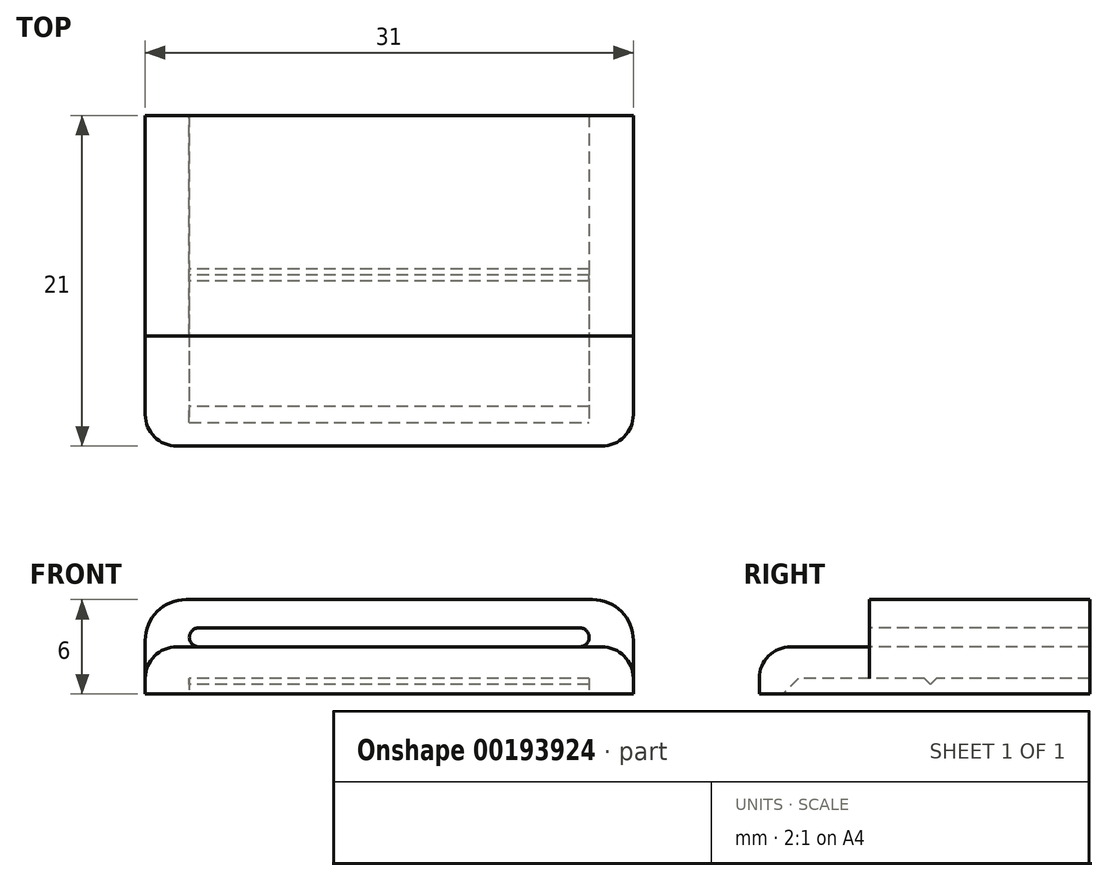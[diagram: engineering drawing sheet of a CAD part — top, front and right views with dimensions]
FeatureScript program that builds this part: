
annotation { "Feature Type Name" : "Feature", "Feature Type Description" : "" }
export const myFeature = defineFeature(function(context is Context, id is Id, definition is map)
    precondition{}
    {
        {
            var Q0;
            Q0=qCreatedBy(makeId("Top.planeOp"),FACE);
            var sketch = newSketch(context, id + "F0", { "sketchPlane" : qUnion([Q0])});
            skLineSegment(sketch, "E0.bottom", {"start": v(15.5, 10.5) * mm, "end": v(-15.5, 10.5) * mm});
            skLineSegment(sketch, "E0.top", {"start": v(15.5, -10.5) * mm, "end": v(-15.5, -10.5) * mm});
            skLineSegment(sketch, "E0.left", {"start": v(15.5, 10.5) * mm, "end": v(15.5, -10.5) * mm});
            skLineSegment(sketch, "E0.right", {"start": v(-15.5, 10.5) * mm, "end": v(-15.5, -10.5) * mm});
            skPoint(sketch, "E0.middle", {"position": v(0, 0) * mm});
            skSolve(sketch);
        }
        {
            var Q0;
            Q0 = qSketchRegion(id + "F0", true);
            extrude(context, id + "F1", {"entities" : qUnion([Q0]), "depth" : 3 * mm});
        }
        {
            var Q0;
            Q0=makeQuery(id+"F1.opExtrude","CAP_FACE",FACE,{"disambiguationData":[OSD([sQuery(id+"F0.wireOp",EDGE,"E0.bottom"),sQuery(id+"F0.wireOp",EDGE,"E0.top"),sQuery(id+"F0.wireOp",EDGE,"E0.left"),sQuery(id+"F0.wireOp",EDGE,"E0.right")])],"isStart":false});
            var sketch = newSketch(context, id + "F2", { "sketchPlane" : qUnion([Q0])});
            skLineSegment(sketch, "E1.bottom", {"start": v(-15.5, 10.5) * mm, "end": v(15.5, 10.5) * mm});
            skLineSegment(sketch, "E1.top", {"start": v(-15.5, -3.5) * mm, "end": v(15.5, -3.5) * mm});
            skLineSegment(sketch, "E1.left", {"start": v(-15.5, 10.5) * mm, "end": v(-15.5, -3.5) * mm});
            skLineSegment(sketch, "E1.right", {"start": v(15.5, 10.5) * mm, "end": v(15.5, -3.5) * mm});
            skSolve(sketch);
        }
        {
            var Q0;
            Q0 = qSketchRegion(id + "F2", true);
            extrude(context, id + "F3", {"entities" : qUnion([Q0]), "operationType" : NewBodyOperationType.ADD, "depth" : 3 * mm});
        }
        {
            var Q0;
            Q0=makeQuery(id+"F3.opExtrude","SWEPT_FACE",FACE,{"disambiguationData":[OSD([sQuery(id+"F2.wireOp",EDGE,"E1.top")])]});
            var sketch = newSketch(context, id + "F4", { "sketchPlane" : qUnion([Q0])});
            skLineSegment(sketch, "E2.bottom", {"start": v(-12.7, 3) * mm, "end": v(12.7, 3) * mm});
            skLineSegment(sketch, "E2.top", {"start": v(-12.7, 4.2) * mm, "end": v(12.7, 4.2) * mm});
            skLineSegment(sketch, "E2.left", {"start": v(-12.7, 3) * mm, "end": v(-12.7, 4.2) * mm});
            skLineSegment(sketch, "E2.right", {"start": v(12.7, 3) * mm, "end": v(12.7, 4.2) * mm});
            skSolve(sketch);
        }
        {
            var Q0;
            Q0 = qSketchRegion(id + "F4", true);
            extrude(context, id + "F5", {"entities" : qUnion([Q0]), "operationType" : NewBodyOperationType.REMOVE, "oppositeDirection" : true, "depth" : 25 * mm});
        }
        {
            var Q0;
            Q0=makeQuery(id+"F1.opExtrude","CAP_FACE",FACE,{"disambiguationData":[OSD([sQuery(id+"F0.wireOp",EDGE,"E0.bottom"),sQuery(id+"F0.wireOp",EDGE,"E0.top"),sQuery(id+"F0.wireOp",EDGE,"E0.left"),sQuery(id+"F0.wireOp",EDGE,"E0.right")])],"isStart":true});
            var sketch = newSketch(context, id + "F6", { "sketchPlane" : qUnion([Q0])});
            skLineSegment(sketch, "E3.bottom", {"start": v(-12.7, -10.5) * mm, "end": v(12.7, -10.5) * mm});
            skLineSegment(sketch, "E3.top", {"start": v(-12.7, 9) * mm, "end": v(12.7, 9) * mm});
            skLineSegment(sketch, "E3.left", {"start": v(-12.7, -10.5) * mm, "end": v(-12.7, 9) * mm});
            skLineSegment(sketch, "E3.right", {"start": v(12.7, -10.5) * mm, "end": v(12.7, 9) * mm});
            skSolve(sketch);
        }
        {
            var Q0;
            Q0 = qSketchRegion(id + "F6", true);
            extrude(context, id + "F7", {"entities" : qUnion([Q0]), "operationType" : NewBodyOperationType.REMOVE, "oppositeDirection" : true, "depth" : 1 * mm});
        }
        {
            var Q0;
            Q0=makeQuery(id+"F5.boolean.opBoolean","COPY",EDGE,{"derivedFrom":makeQuery(id+"F5.opExtrude","SWEPT_EDGE",EDGE,{"disambiguationData":[OSD([sQuery(id+"F4.wireOp",EDGE,"E2.top"),sQuery(id+"F4.wireOp",EDGE,"E2.right")])]})});
            var Q1;
            Q1=makeQuery(id+"F5.boolean.opBoolean","COPY",EDGE,{"derivedFrom":makeQuery(id+"F5.opExtrude","SWEPT_EDGE",EDGE,{"disambiguationData":[OSD([sQuery(id+"F2.wireOp",EDGE,"E1.top"),sQuery(id+"F4.wireOp",EDGE,"E2.bottom"),sQuery(id+"F4.wireOp",EDGE,"E2.right")])]})});
            var Q2;
            Q2=makeQuery(id+"F5.boolean.opBoolean","COPY",EDGE,{"derivedFrom":makeQuery(id+"F5.opExtrude","SWEPT_EDGE",EDGE,{"disambiguationData":[OSD([sQuery(id+"F2.wireOp",EDGE,"E1.top"),sQuery(id+"F4.wireOp",EDGE,"E2.bottom"),sQuery(id+"F4.wireOp",EDGE,"E2.left")])]})});
            var Q3;
            Q3=makeQuery(id+"F5.boolean.opBoolean","COPY",EDGE,{"derivedFrom":makeQuery(id+"F5.opExtrude","SWEPT_EDGE",EDGE,{"disambiguationData":[OSD([sQuery(id+"F4.wireOp",EDGE,"E2.top"),sQuery(id+"F4.wireOp",EDGE,"E2.left")])]})});
            fillet(context, id + "F8", {"entities" : qUnion([Q0, Q1, Q2, Q3]), "radius" : 0.6 * mm, "tangentPropagation" : true, "allowEdgeOverflow" : false});
        }
        {
            var Q0;
            Q0=makeQuery(id+"F3.opExtrude","CAP_EDGE",EDGE,{"disambiguationData":[OSD([sQuery(id+"F2.wireOp",EDGE,"E1.left")])],"isStart":false});
            var Q1;
            Q1=makeQuery(id+"F3.opExtrude","CAP_EDGE",EDGE,{"disambiguationData":[OSD([sQuery(id+"F2.wireOp",EDGE,"E1.right")])],"isStart":false});
            fillet(context, id + "F9", {"entities" : qUnion([Q0, Q1]), "radius" : 2.6 * mm, "tangentPropagation" : true, "allowEdgeOverflow" : false});
        }
        {
            var Q0;
            Q0=makeQuery(id+"F7.boolean.opBoolean","COPY",FACE,{"derivedFrom":makeQuery(id+"F7.opExtrude","CAP_FACE",FACE,{"disambiguationData":[OSD([sQuery(id+"F6.wireOp",EDGE,"E3.bottom"),sQuery(id+"F6.wireOp",EDGE,"E3.top"),sQuery(id+"F6.wireOp",EDGE,"E3.left"),sQuery(id+"F6.wireOp",EDGE,"E3.right")])],"isStart":false})});
            var sketch = newSketch(context, id + "F10", { "sketchPlane" : qUnion([Q0])});
            skLineSegment(sketch, "E4.bottom", {"start": v(12.7, -0.75) * mm, "end": v(-12.7, -0.75) * mm});
            skLineSegment(sketch, "E4.top", {"start": v(12.7, 0) * mm, "end": v(-12.7, 0) * mm});
            skLineSegment(sketch, "E4.left", {"start": v(12.7, -0.75) * mm, "end": v(12.7, 0) * mm});
            skLineSegment(sketch, "E4.right", {"start": v(-12.7, -0.75) * mm, "end": v(-12.7, 0) * mm});
            skSolve(sketch);
        }
        {
            var Q0;
            Q0 = qSketchRegion(id + "F10", true);
            extrude(context, id + "F11", {"entities" : qUnion([Q0]), "operationType" : NewBodyOperationType.ADD, "depth" : 0.5 * mm});
        }
        {
            var Q0;
            Q0=makeQuery(id+"F11.opExtrude","CAP_EDGE",EDGE,{"disambiguationData":[OSD([sQuery(id+"F10.wireOp",EDGE,"E4.top")])],"isStart":false});
            var Q1;
            Q1=makeQuery(id+"F11.opExtrude","CAP_EDGE",EDGE,{"disambiguationData":[OSD([sQuery(id+"F10.wireOp",EDGE,"E4.bottom")])],"isStart":false});
            chamfer(context, id + "F12", {"entities" : qUnion([Q0, Q1]), "width" : 0.5 * mm, "tangentPropagation" : true});
        }
        {
            var Q0;
            Q0=makeQuery(id+"F1.opExtrude","SWEPT_EDGE",EDGE,{"disambiguationData":[OSD([sQuery(id+"F0.wireOp",EDGE,"E0.top"),sQuery(id+"F0.wireOp",EDGE,"E0.left")])]});
            var Q1;
            Q1=makeQuery(id+"F1.opExtrude","SWEPT_EDGE",EDGE,{"disambiguationData":[OSD([sQuery(id+"F0.wireOp",EDGE,"E0.top"),sQuery(id+"F0.wireOp",EDGE,"E0.right")])]});
            fillet(context, id + "F13", {"entities" : qUnion([Q0, Q1]), "radius" : 2 * mm, "tangentPropagation" : true, "allowEdgeOverflow" : false});
        }
        {
            var Q0;
            Q0=makeQuery(id+"F7.boolean.opBoolean","COPY",EDGE,{"derivedFrom":makeQuery(id+"F7.opExtrude","CAP_EDGE",EDGE,{"disambiguationData":[OSD([sQuery(id+"F6.wireOp",EDGE,"E3.top")])],"isStart":false})});
            chamfer(context, id + "F14", {"entities" : qUnion([Q0]), "width" : 1 * mm, "tangentPropagation" : true});
        }
        {
            var Q0;
            Q0=makeQuery(id+"F1.opExtrude","CAP_EDGE",EDGE,{"disambiguationData":[OSD([sQuery(id+"F0.wireOp",EDGE,"E0.top")])],"isStart":false});
            fillet(context, id + "F15", {"entities" : qUnion([Q0]), "radius" : 2 * mm, "tangentPropagation" : true, "allowEdgeOverflow" : false});
        }
    });
